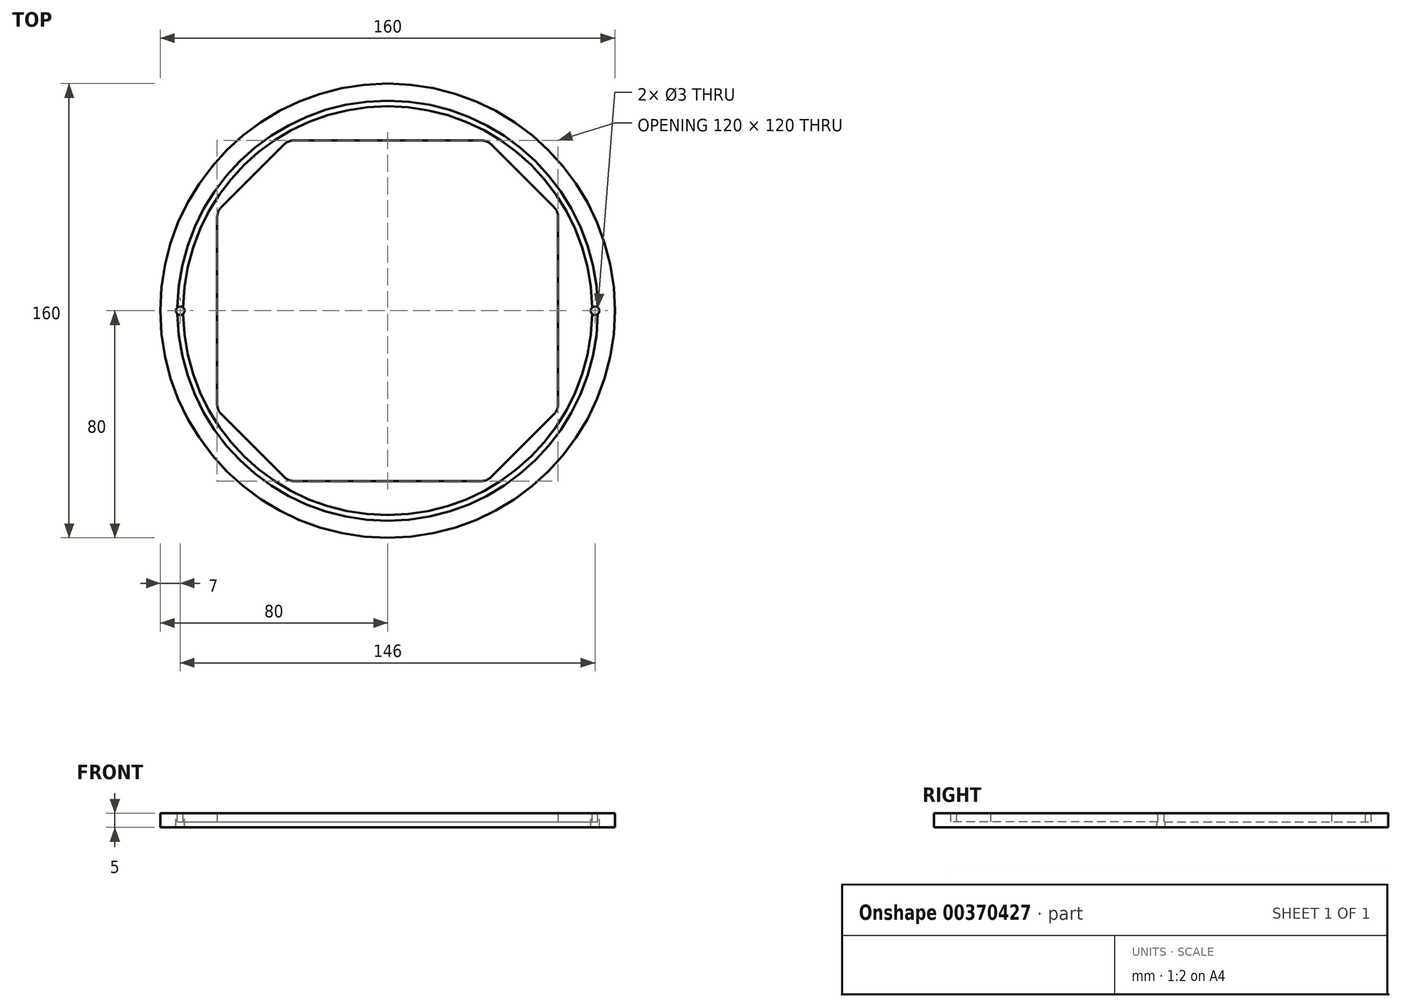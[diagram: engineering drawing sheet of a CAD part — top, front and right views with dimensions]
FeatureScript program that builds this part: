
annotation { "Feature Type Name" : "Feature", "Feature Type Description" : "" }
export const myFeature = defineFeature(function(context is Context, id is Id, definition is map)
    precondition{}
    {
        {
            var Q0;
            Q0=qCreatedBy(makeId("Top.planeOp"),FACE);
            var sketch = newSketch(context, id + "F0", { "sketchPlane" : qUnion([Q0])});
            skLineSegment(sketch, "E0", {"start": v(60, -25) * mm, "end": v(60, -95) * mm});
            skLineSegment(sketch, "E1", {"start": v(60, -95) * mm, "end": v(35, -120) * mm});
            skLineSegment(sketch, "E2", {"start": v(35, -120) * mm, "end": v(-35, -120) * mm});
            skLineSegment(sketch, "E3", {"start": v(-35, -120) * mm, "end": v(-60, -95) * mm});
            skLineSegment(sketch, "E4", {"start": v(-60, -95) * mm, "end": v(-60, -25) * mm});
            skLineSegment(sketch, "E5", {"start": v(-60, -25) * mm, "end": v(-35, 0) * mm});
            skLineSegment(sketch, "E6", {"start": v(-35, 0) * mm, "end": v(35, 0) * mm});
            skLineSegment(sketch, "E7", {"start": v(35, 0) * mm, "end": v(60, -25) * mm});
            skCircle(sketch, "E8", {"center": v(0, -60) * mm, "radius": 80 * mm});
            skPoint(sketch, "E8.centerSnap0", {"position": v(60, -60) * mm});
            skSolve(sketch);
        }
        {
            var Q0;
            Q0=makeQuery(id+"F0.imprint","IMPRINT",FACE,{"disambiguationData":[TD([[makeQuery(id+"F0.imprint","IMPRINT",EDGE,{"derivedFrom":sQuery(id+"F0.wireOp",EDGE,"E0")}),1.0]])]});
            extrude(context, id + "F1", {"entities" : qUnion([Q0]), "depth" : 5 * mm});
        }
        {
            var Q0;
            Q0=makeQuery(id+"F1.opExtrude","CAP_FACE",FACE,{"disambiguationData":[OSD([sQuery(id+"F0.wireOp",EDGE,"E0"),sQuery(id+"F0.wireOp",EDGE,"E1"),sQuery(id+"F0.wireOp",EDGE,"E2"),sQuery(id+"F0.wireOp",EDGE,"E3"),sQuery(id+"F0.wireOp",EDGE,"E4"),sQuery(id+"F0.wireOp",EDGE,"E5"),sQuery(id+"F0.wireOp",EDGE,"E6"),sQuery(id+"F0.wireOp",EDGE,"E7"),sQuery(id+"F0.wireOp",EDGE,"E8")])],"isStart":false});
            var sketch = newSketch(context, id + "F2", { "sketchPlane" : qUnion([Q0])});
            skCircle(sketch, "E9", {"center": v(0, -60) * mm, "radius": 72 * mm});
            skCircle(sketch, "E10.0", {"center": v(0, -60) * mm, "radius": 74 * mm});
            skPoint(sketch, "E11", {"position": v(-73, -60) * mm});
            skPoint(sketch, "E11.positionSnap0", {"position": v(-60, -60) * mm});
            skPoint(sketch, "E12", {"position": v(73, -60) * mm});
            skPoint(sketch, "E12.positionSnap0", {"position": v(60, -60) * mm});
            skSolve(sketch);
        }
        {
            var Q0;
            Q0 = qSketchRegion(id + "F2", true);
            extrude(context, id + "F3", {"entities" : qUnion([Q0]), "operationType" : NewBodyOperationType.REMOVE, "oppositeDirection" : true, "depth" : 3 * mm});
        }
        {
            var Q0;
            Q0=sQuery(id+"F2.wireOp",VERTEX,"E11");
            var Q1;
            Q1=sQuery(id+"F2.wireOp",VERTEX,"E12");
            var Q2;
            Q2=makeQuery(id+"F1.opExtrude","SWEPT_BODY",BODY,{"disambiguationData":[OSD([sQuery(id+"F0.wireOp",EDGE,"E0"),sQuery(id+"F0.wireOp",EDGE,"E1"),sQuery(id+"F0.wireOp",EDGE,"E2"),sQuery(id+"F0.wireOp",EDGE,"E3"),sQuery(id+"F0.wireOp",EDGE,"E4"),sQuery(id+"F0.wireOp",EDGE,"E5"),sQuery(id+"F0.wireOp",EDGE,"E6"),sQuery(id+"F0.wireOp",EDGE,"E7"),sQuery(id+"F0.wireOp",EDGE,"E8")])]});
            hole(context, id + "F4", {"style" : HoleStyle.SIMPLE, "endStyle" : HoleEndStyle.THROUGH, "holeDiameter" : 3 * mm, "isTappedThrough" : true, "tappedDepth" : 12 * mm, "tapClearance" : 3, "locations" : qUnion([Q0, Q1]), "scope" : qUnion([Q2])});
        }
        {
            var Q0;
            Q0=makeQuery(id+"F1.opExtrude","SWEPT_EDGE",EDGE,{"disambiguationData":[OSD([sQuery(id+"F0.wireOp",EDGE,"E5"),sQuery(id+"F0.wireOp",EDGE,"E6")])]});
            var Q1;
            Q1=makeQuery(id+"F1.opExtrude","SWEPT_EDGE",EDGE,{"disambiguationData":[OSD([sQuery(id+"F0.wireOp",EDGE,"E6"),sQuery(id+"F0.wireOp",EDGE,"E7")])]});
            var Q2;
            Q2=makeQuery(id+"F1.opExtrude","SWEPT_EDGE",EDGE,{"disambiguationData":[OSD([sQuery(id+"F0.wireOp",EDGE,"E4"),sQuery(id+"F0.wireOp",EDGE,"E5")])]});
            var Q3;
            Q3=makeQuery(id+"F1.opExtrude","SWEPT_EDGE",EDGE,{"disambiguationData":[OSD([sQuery(id+"F0.wireOp",EDGE,"E0"),sQuery(id+"F0.wireOp",EDGE,"E7")])]});
            var Q4;
            Q4=makeQuery(id+"F1.opExtrude","SWEPT_EDGE",EDGE,{"disambiguationData":[OSD([sQuery(id+"F0.wireOp",EDGE,"E0"),sQuery(id+"F0.wireOp",EDGE,"E1")])]});
            var Q5;
            Q5=makeQuery(id+"F1.opExtrude","SWEPT_EDGE",EDGE,{"disambiguationData":[OSD([sQuery(id+"F0.wireOp",EDGE,"E1"),sQuery(id+"F0.wireOp",EDGE,"E2")])]});
            var Q6;
            Q6=makeQuery(id+"F1.opExtrude","SWEPT_EDGE",EDGE,{"disambiguationData":[OSD([sQuery(id+"F0.wireOp",EDGE,"E2"),sQuery(id+"F0.wireOp",EDGE,"E3")])]});
            var Q7;
            Q7=makeQuery(id+"F1.opExtrude","SWEPT_EDGE",EDGE,{"disambiguationData":[OSD([sQuery(id+"F0.wireOp",EDGE,"E3"),sQuery(id+"F0.wireOp",EDGE,"E4")])]});
            fillet(context, id + "F5", {"entities" : qUnion([Q0, Q1, Q2, Q3, Q4, Q5, Q6, Q7]), "radius" : 5 * mm, "tangentPropagation" : true, "allowEdgeOverflow" : false});
        }
    });
